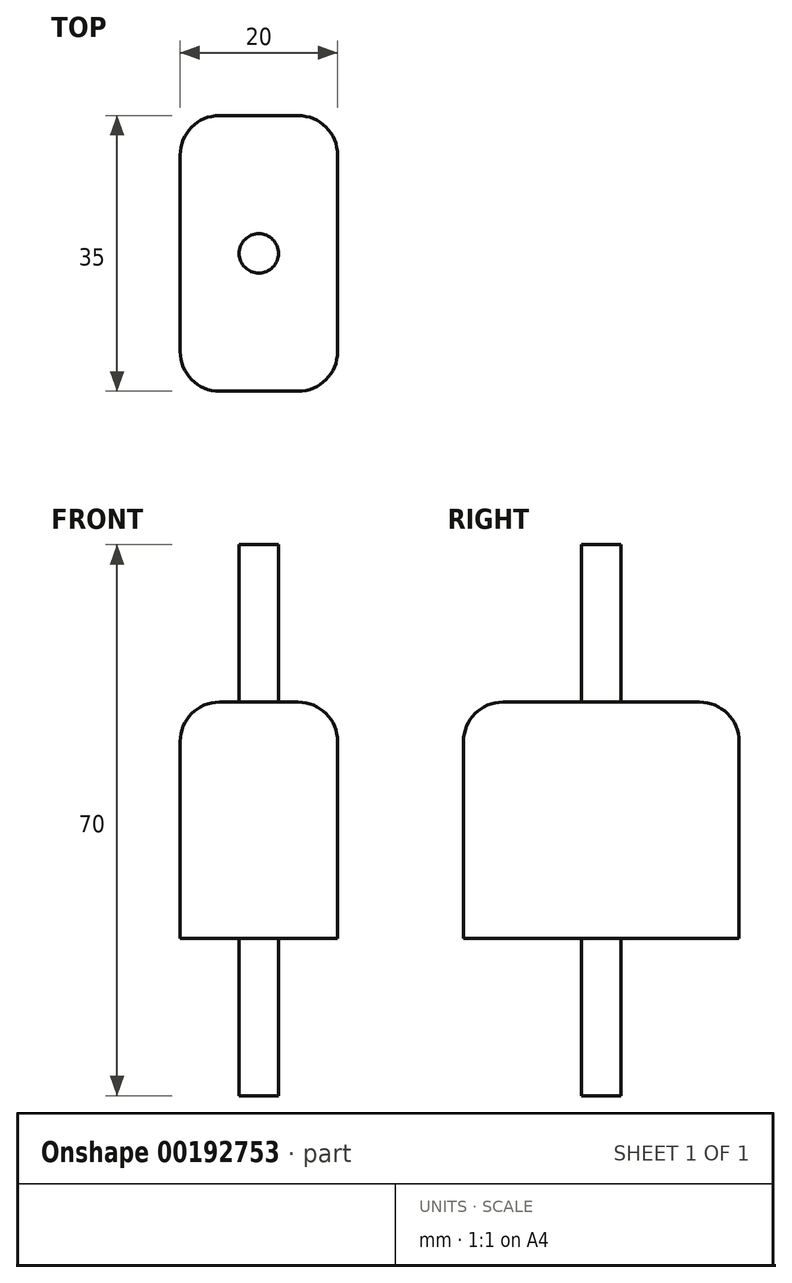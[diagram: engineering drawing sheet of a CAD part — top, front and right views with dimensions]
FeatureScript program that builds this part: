
annotation { "Feature Type Name" : "Feature", "Feature Type Description" : "" }
export const myFeature = defineFeature(function(context is Context, id is Id, definition is map)
    precondition{}
    {
        {
            var Q0;
            Q0=qCreatedBy(makeId("Top.planeOp"),FACE);
            var sketch = newSketch(context, id + "F0", { "sketchPlane" : qUnion([Q0])});
            skLineSegment(sketch, "E0.bottom", {"start": v(10, -17.5) * mm, "end": v(-10, -17.5) * mm});
            skLineSegment(sketch, "E0.top", {"start": v(10, 17.5) * mm, "end": v(-10, 17.5) * mm});
            skLineSegment(sketch, "E0.left", {"start": v(10, -17.5) * mm, "end": v(10, 17.5) * mm});
            skLineSegment(sketch, "E0.right", {"start": v(-10, -17.5) * mm, "end": v(-10, 17.5) * mm});
            skPoint(sketch, "E0.middle", {"position": v(0, 0) * mm});
            skSolve(sketch);
        }
        {
            var Q0;
            Q0=makeQuery(id+"F0.imprint","IMPRINT",FACE,{"disambiguationData":[TD([[makeQuery(id+"F0.imprint","IMPRINT",EDGE,{"derivedFrom":sQuery(id+"F0.wireOp",EDGE,"E0.bottom")}),-1.0]])]});
            extrude(context, id + "F1", {"entities" : qUnion([Q0]), "depth" : 30 * mm});
        }
        {
            var Q0;
            Q0=makeQuery(id+"F1.opExtrude","CAP_FACE",FACE,{"disambiguationData":[OSD([sQuery(id+"F0.wireOp",EDGE,"E0.bottom"),sQuery(id+"F0.wireOp",EDGE,"E0.top"),sQuery(id+"F0.wireOp",EDGE,"E0.left"),sQuery(id+"F0.wireOp",EDGE,"E0.right")])],"isStart":false});
            var sketch = newSketch(context, id + "F2", { "sketchPlane" : qUnion([Q0])});
            skCircle(sketch, "E1", {"center": v(0, 0) * mm, "radius": 2.5 * mm});
            skSolve(sketch);
        }
        {
            var Q0;
            Q0 = qSketchRegion(id + "F2", true);
            extrude(context, id + "F3", {"entities" : qUnion([Q0]), "operationType" : NewBodyOperationType.ADD, "depth" : 20 * mm});
        }
        {
            var Q0;
            Q0=makeQuery(id+"F1.opExtrude","CAP_EDGE",EDGE,{"disambiguationData":[OSD([sQuery(id+"F0.wireOp",EDGE,"E0.bottom")])],"isStart":false});
            var Q1;
            Q1=makeQuery(id+"F1.opExtrude","SWEPT_EDGE",EDGE,{"disambiguationData":[OSD([sQuery(id+"F0.wireOp",EDGE,"E0.bottom"),sQuery(id+"F0.wireOp",EDGE,"E0.left")])]});
            var Q2;
            Q2=makeQuery(id+"F1.opExtrude","SWEPT_EDGE",EDGE,{"disambiguationData":[OSD([sQuery(id+"F0.wireOp",EDGE,"E0.bottom"),sQuery(id+"F0.wireOp",EDGE,"E0.right")])]});
            var Q3;
            Q3=makeQuery(id+"F1.opExtrude","CAP_EDGE",EDGE,{"disambiguationData":[OSD([sQuery(id+"F0.wireOp",EDGE,"E0.right")])],"isStart":false});
            var Q4;
            Q4=makeQuery(id+"F1.opExtrude","CAP_EDGE",EDGE,{"disambiguationData":[OSD([sQuery(id+"F0.wireOp",EDGE,"E0.top")])],"isStart":false});
            var Q5;
            Q5=makeQuery(id+"F1.opExtrude","CAP_EDGE",EDGE,{"disambiguationData":[OSD([sQuery(id+"F0.wireOp",EDGE,"E0.left")])],"isStart":false});
            var Q6;
            Q6=makeQuery(id+"F1.opExtrude","SWEPT_EDGE",EDGE,{"disambiguationData":[OSD([sQuery(id+"F0.wireOp",EDGE,"E0.top"),sQuery(id+"F0.wireOp",EDGE,"E0.left")])]});
            var Q7;
            Q7=makeQuery(id+"F1.opExtrude","SWEPT_EDGE",EDGE,{"disambiguationData":[OSD([sQuery(id+"F0.wireOp",EDGE,"E0.top"),sQuery(id+"F0.wireOp",EDGE,"E0.right")])]});
            fillet(context, id + "F4", {"entities" : qUnion([Q0, Q1, Q2, Q3, Q4, Q5, Q6, Q7]), "radius" : 5 * mm, "tangentPropagation" : true, "allowEdgeOverflow" : false});
        }
        {
            var Q0;
            Q0=makeQuery(id+"F1.opExtrude","CAP_FACE",FACE,{"disambiguationData":[OSD([sQuery(id+"F0.wireOp",EDGE,"E0.bottom"),sQuery(id+"F0.wireOp",EDGE,"E0.top"),sQuery(id+"F0.wireOp",EDGE,"E0.left"),sQuery(id+"F0.wireOp",EDGE,"E0.right")])],"isStart":true});
            var sketch = newSketch(context, id + "F5", { "sketchPlane" : qUnion([Q0])});
            skCircle(sketch, "E2", {"center": v(0, 0) * mm, "radius": 2.5 * mm});
            skSolve(sketch);
        }
        {
            var Q0;
            Q0 = qSketchRegion(id + "F5", true);
            extrude(context, id + "F6", {"entities" : qUnion([Q0]), "operationType" : NewBodyOperationType.ADD, "depth" : 20 * mm});
        }
    });
